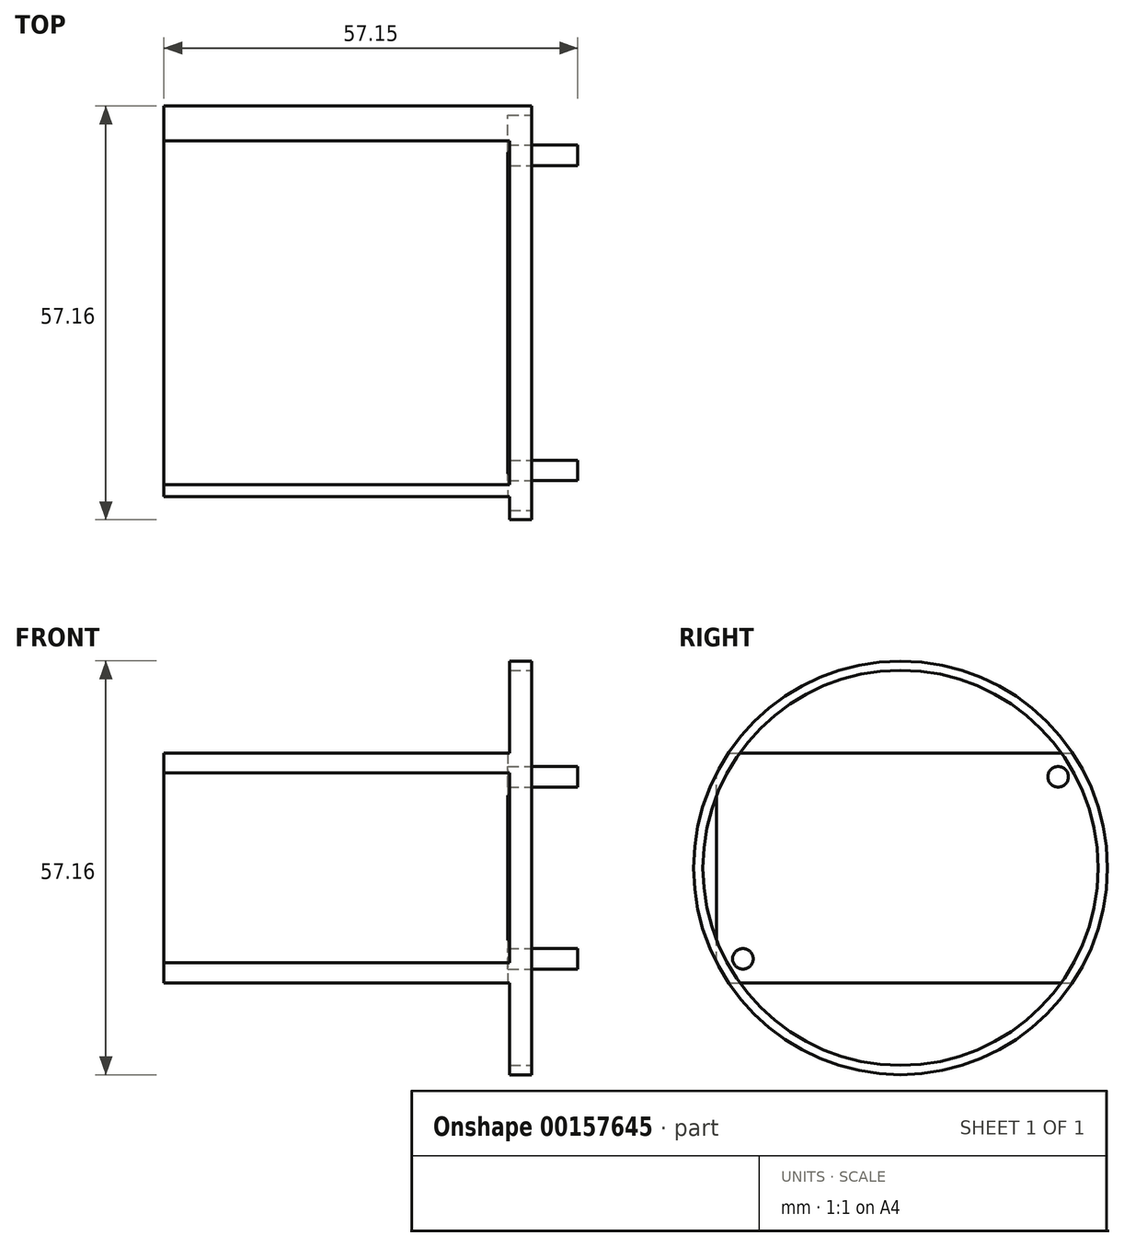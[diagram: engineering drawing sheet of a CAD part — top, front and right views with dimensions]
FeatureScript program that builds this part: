
annotation { "Feature Type Name" : "Feature", "Feature Type Description" : "" }
export const myFeature = defineFeature(function(context is Context, id is Id, definition is map)
    precondition{}
    {
        {
            var Q0;
            Q0=qCreatedBy(makeId("Right.planeOp"),FACE);
            var sketch = newSketch(context, id + "F0", { "sketchPlane" : qUnion([Q0])});
            skCircle(sketch, "E0", {"center": v(0, 0) * mm, "radius": 28.58 * mm});
            skCircle(sketch, "E1", {"center": v(0, 0) * mm, "radius": 27.3 * mm});
            skSolve(sketch);
        }
        {
            var Q0;
            Q0=makeQuery(id+"F0.imprint","IMPRINT",FACE,{"disambiguationData":[TD([[makeQuery(id+"F0.imprint","IMPRINT",EDGE,{"derivedFrom":sQuery(id+"F0.wireOp",EDGE,"E0")}),1.0]])]});
            var Q1;
            Q1=makeQuery(id+"F0.imprint","IMPRINT",FACE,{"disambiguationData":[TD([[makeQuery(id+"F0.imprint","IMPRINT",EDGE,{"derivedFrom":sQuery(id+"F0.wireOp",EDGE,"E1")}),1.0]])]});
            extrude(context, id + "F1", {"entities" : qUnion([Q0, Q1]), "oppositeDirection" : true, "depth" : 57.15 * mm});
        }
        {
            var Q0;
            Q0=makeQuery(id+"F0.imprint","IMPRINT",FACE,{"disambiguationData":[TD([[makeQuery(id+"F0.imprint","IMPRINT",EDGE,{"derivedFrom":sQuery(id+"F0.wireOp",EDGE,"E0")}),1.0]])]});
            extrude(context, id + "F2", {"entities" : qUnion([Q0]), "operationType" : NewBodyOperationType.REMOVE, "oppositeDirection" : true, "depth" : 6.35 * mm});
        }
        {
            var Q0;
            Q0=makeQuery(id+"F1.opExtrude","CAP_FACE",FACE,{"disambiguationData":[OSD([sQuery(id+"F0.wireOp",EDGE,"E0")])],"isStart":false});
            var sketch = newSketch(context, id + "F3", { "sketchPlane" : qUnion([Q0])});
            skLineSegment(sketch, "E2", {"start": v(0, 0) * mm, "end": v(25.4, 0) * mm, "construction": true});
            skLineSegment(sketch, "E3", {"start": v(25.4, 0) * mm, "end": v(25.4, -15.88) * mm, "construction": true});
            skLineSegment(sketch, "E4", {"start": v(25.4, -13.1) * mm, "end": v(25.4, 13.1) * mm});
            skLineSegment(sketch, "E5", {"start": v(25.4, -15.88) * mm, "end": v(1.85, -15.88) * mm, "construction": true});
            skLineSegment(sketch, "E6", {"start": v(23.76, -15.88) * mm, "end": v(-23.76, -15.88) * mm});
            skLineSegment(sketch, "E7.MirrorCS", {"start": v(23.76, 15.88) * mm, "end": v(-23.76, 15.88) * mm});
            skSolve(sketch);
        }
        {
            var Q0;
            {var subQ0=sQuery(id+"F3.wireOp",EDGE,"E6");Q0=makeQuery(id+"F3.imprint","IMPRINT",FACE,{"disambiguationData":[TD([[makeQuery(id+"F3.imprint","IMPRINT",EDGE,{"derivedFrom":subQ0}),1.0]])]});}
            var Q1;
            {var subQ0=sQuery(id+"F3.wireOp",EDGE,"E4");Q1=makeQuery(id+"F3.imprint","IMPRINT",FACE,{"disambiguationData":[TD([[makeQuery(id+"F3.imprint","IMPRINT",EDGE,{"derivedFrom":subQ0}),-1.0]])]});}
            var Q2;
            {var subQ0=sQuery(id+"F3.wireOp",EDGE,"E7.MirrorCS");Q2=makeQuery(id+"F3.imprint","IMPRINT",FACE,{"disambiguationData":[TD([[makeQuery(id+"F3.imprint","IMPRINT",EDGE,{"derivedFrom":subQ0}),-1.0]])]});}
            extrude(context, id + "F4", {"entities" : qUnion([Q0, Q1, Q2]), "operationType" : NewBodyOperationType.REMOVE, "oppositeDirection" : true, "depth" : 47.75 * mm});
        }
        {
            var Q0;
            Q0=makeQuery(id+"F1.opExtrude","CAP_FACE",FACE,{"disambiguationData":[OSD([sQuery(id+"F0.wireOp",EDGE,"E0")])],"isStart":true});
            var sketch = newSketch(context, id + "F5", { "sketchPlane" : qUnion([Q0])});
            skCircle(sketch, "E8", {"center": v(-21.77, 12.57) * mm, "radius": 1.42 * mm});
            skCircle(sketch, "E9.MirrorC", {"center": v(-21.77, -12.57) * mm, "radius": 1.42 * mm});
            skCircle(sketch, "E10.MirrorC", {"center": v(21.77, 12.57) * mm, "radius": 1.42 * mm});
            skCircle(sketch, "E11.MirrorC", {"center": v(21.77, -12.57) * mm, "radius": 1.42 * mm});
            skSolve(sketch);
        }
        {
            var Q0;
            Q0=makeQuery(id+"F5.imprint","IMPRINT",FACE,{"disambiguationData":[TD([[makeQuery(id+"F5.imprint","IMPRINT",EDGE,{"derivedFrom":sQuery(id+"F5.wireOp",EDGE,"E8")}),1.0]])]});
            var Q1;
            Q1=makeQuery(id+"F5.imprint","IMPRINT",FACE,{"disambiguationData":[TD([[makeQuery(id+"F5.imprint","IMPRINT",EDGE,{"derivedFrom":sQuery(id+"F5.wireOp",EDGE,"E10.MirrorC")}),-1.0]])]});
            var Q2;
            Q2=makeQuery(id+"F5.imprint","IMPRINT",FACE,{"disambiguationData":[TD([[makeQuery(id+"F5.imprint","IMPRINT",EDGE,{"derivedFrom":sQuery(id+"F5.wireOp",EDGE,"E11.MirrorC")}),1.0]])]});
            var Q3;
            Q3=makeQuery(id+"F5.imprint","IMPRINT",FACE,{"disambiguationData":[TD([[makeQuery(id+"F5.imprint","IMPRINT",EDGE,{"derivedFrom":sQuery(id+"F5.wireOp",EDGE,"E9.MirrorC")}),-1.0]])]});
            extrude(context, id + "F6", {"entities" : qUnion([Q0, Q1, Q2, Q3]), "operationType" : NewBodyOperationType.REMOVE, "oppositeDirection" : true, "depth" : 9.65 * mm});
        }
    });
